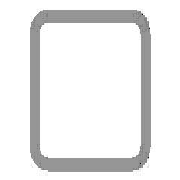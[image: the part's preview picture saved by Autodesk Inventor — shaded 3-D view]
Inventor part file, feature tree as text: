
AUTODESK INVENTOR PART (.ipt)
format: ipt  version: 2025 (Build 290162010, 162A)  size: 133,632 bytes
history: native  units: mm (DEFAULTED — no unit token found)
features: other x4, sketch x1, plane x1
ambient origin geometry x8: Origin, YZ Plane, XZ Plane, XY Plane, X Axis, Y Axis, Z Axis, Center Point
bodies: Solid1 (feature_tree), Body (feature_tree)
feature tree (6):
  parser-record x1  (decoder bookkeeping rows leaked as tree rows — omitted from the tree; the rows remain in map.json)
  other  "Driven Length"
  other  "Start Plane"
  other  "End Plane"
  sketch  "Sketch3"  dims[d3=710.0mm d4=0.0mm d7=4.0mm d9=40.0mm d11=40.0mm d12=2.0mm d13=-0.0mm d14=710.0mm d15=20.0mm d16=20.0mm d17=90.0deg d18=710.0mm]
  plane  "Work Plane3"
